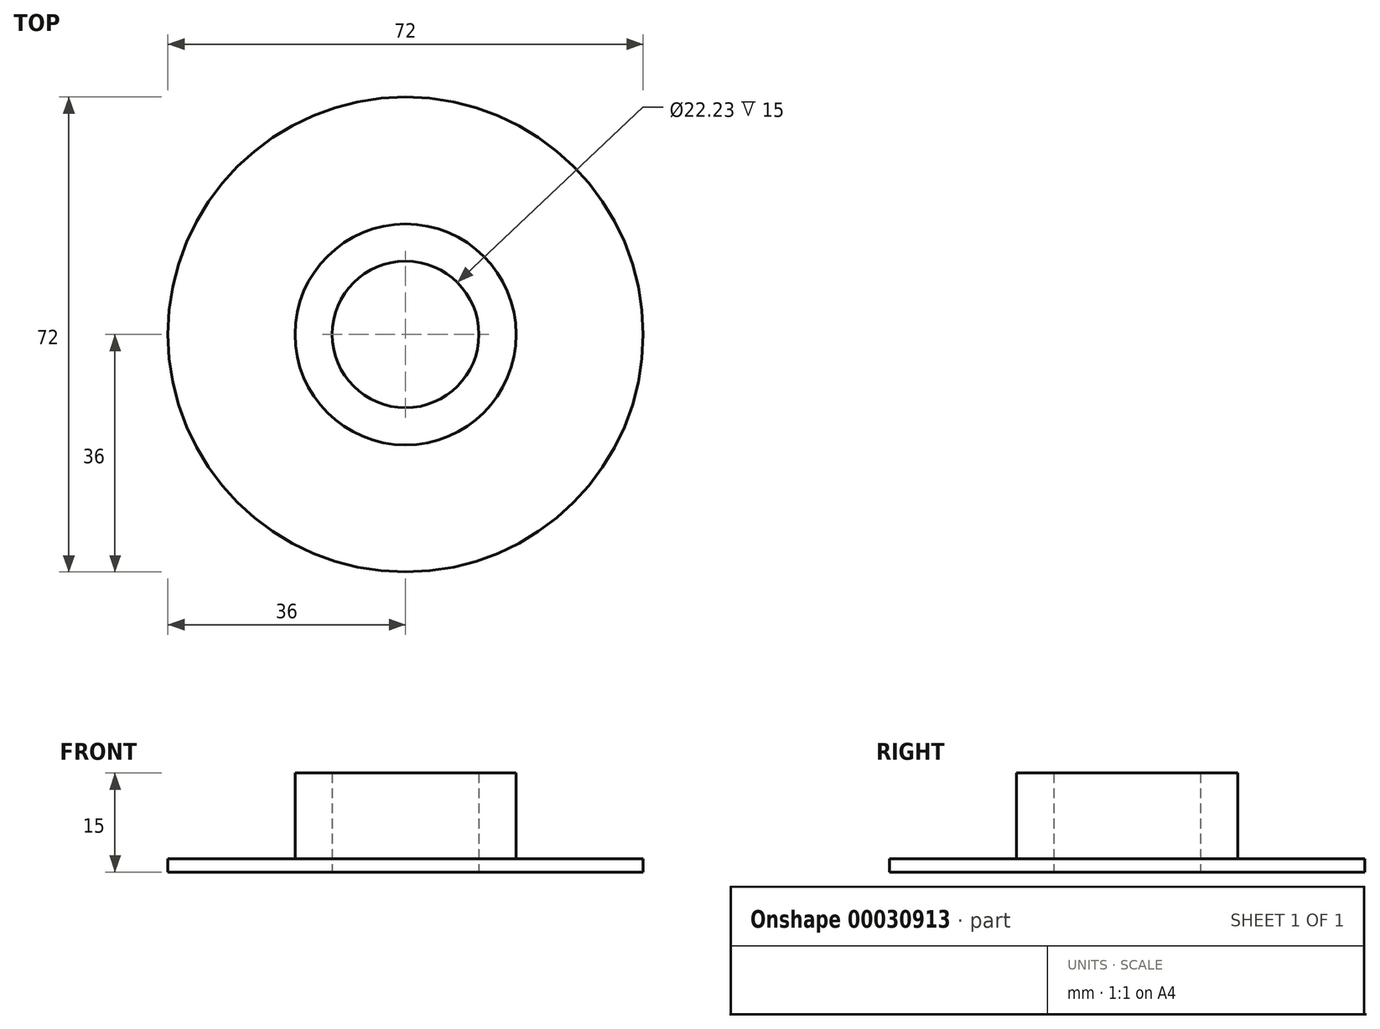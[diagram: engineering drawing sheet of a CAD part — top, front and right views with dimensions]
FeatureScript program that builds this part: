
annotation { "Feature Type Name" : "Feature", "Feature Type Description" : "" }
export const myFeature = defineFeature(function(context is Context, id is Id, definition is map)
    precondition{}
    {
        {
            var Q0;
            Q0=qCreatedBy(makeId("Top.planeOp"),FACE);
            var sketch = newSketch(context, id + "F0", { "sketchPlane" : qUnion([Q0])});
            skCircle(sketch, "E0", {"center": v(0, 0) * mm, "radius": 36 * mm});
            skCircle(sketch, "E1", {"center": v(0, 0) * mm, "radius": 16.75 * mm});
            skCircle(sketch, "E2", {"center": v(0, 0) * mm, "radius": 11.12 * mm});
            skSolve(sketch);
        }
        {
            var Q0;
            Q0=makeQuery(id+"F0.imprint","IMPRINT",FACE,{"disambiguationData":[TD([[makeQuery(id+"F0.imprint","IMPRINT",EDGE,{"derivedFrom":sQuery(id+"F0.wireOp",EDGE,"E1")}),1.0]])]});
            var sketch = newSketch(context, id + "F1", { "sketchPlane" : qUnion([Q0])});
            skSolve(sketch);
        }
        {
            var Q0;
            Q0 = qSketchRegion(id + "F1", true);
            var Q1;
            Q1=makeQuery(id+"F0.imprint","IMPRINT",FACE,{"disambiguationData":[TD([[makeQuery(id+"F0.imprint","IMPRINT",EDGE,{"derivedFrom":sQuery(id+"F0.wireOp",EDGE,"E0")}),1.0]])]});
            extrude(context, id + "F2", {"entities" : qUnion([Q0, Q1]), "depth" : 2 * mm});
        }
        {
            var Q0;
            Q0 = qSketchRegion(id + "F1", true);
            var Q1;
            Q1=makeQuery(id+"F1.imprint","IMPRINT",FACE,{"disambiguationData":[TD([[makeQuery(id+"F1.imprint","IMPRINT",EDGE,{"derivedFrom":makeQuery(id+"F0.imprint","IMPRINT",EDGE,{"derivedFrom":sQuery(id+"F0.wireOp",EDGE,"E1")})}),1.0]])]});
            extrude(context, id + "F3", {"entities" : qUnion([Q0, Q1]), "operationType" : NewBodyOperationType.ADD, "depth" : 15 * mm});
        }
    });
